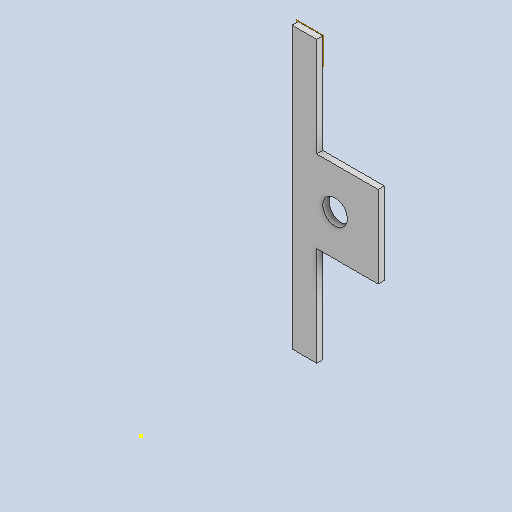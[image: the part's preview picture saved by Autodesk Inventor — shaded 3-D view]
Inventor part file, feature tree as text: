
AUTODESK INVENTOR PART (.ipt)
format: ipt  version: 2023.1 (Build 271208000, 208)  size: 167,424 bytes
history: native  units: mm
features: sketch x5, other x4, extrude x3, reference x2, projected_geometry x2, plane x1
ambient origin geometry x8: Origin, YZ Plane, XZ Plane, XY Plane, X Axis, Y Axis, Z Axis, Center Point
bodies: Solid1 (feature_tree)
feature tree (17):
  sketch  "Sketch1"  dims[d0=3.0mm d1=0.0mm d9=3.0mm]
  plane  "Work Plane1"
  extrude  "Extrusion1"  Depth=3.0mm
  extrude  "Extrusion4"  Depth=30.0mm TaperAngle=0.0deg
  sketch  "Sketch6"  dims[d15=30.0mm d16=0.0mm]
  extrude  "Extrusion5"  Depth=12.0mm
  sketch  "Sketch2"  dims[d10=40.0mm d11=30.0mm d12=0.0mm]
  reference  "Reference1"
  reference  "Reference2"
  sketch  "Sketch5"  dims[d13=12.0mm d14=9.0mm]
  projected_geometry  "Projected Loop3"
  sketch  "Sketch7"
  projected_geometry  "Projected Loop4"
  parser-record x1  (decoder bookkeeping rows leaked as tree rows — omitted from the tree; the rows remain in map.json)
  other  "Main Assembly.iam"
  other  "12 mm rod:1"
  other  "12 mm rod:2"
note: 1 file-system path scrubbed to <path> (originals preserved in map.json)
